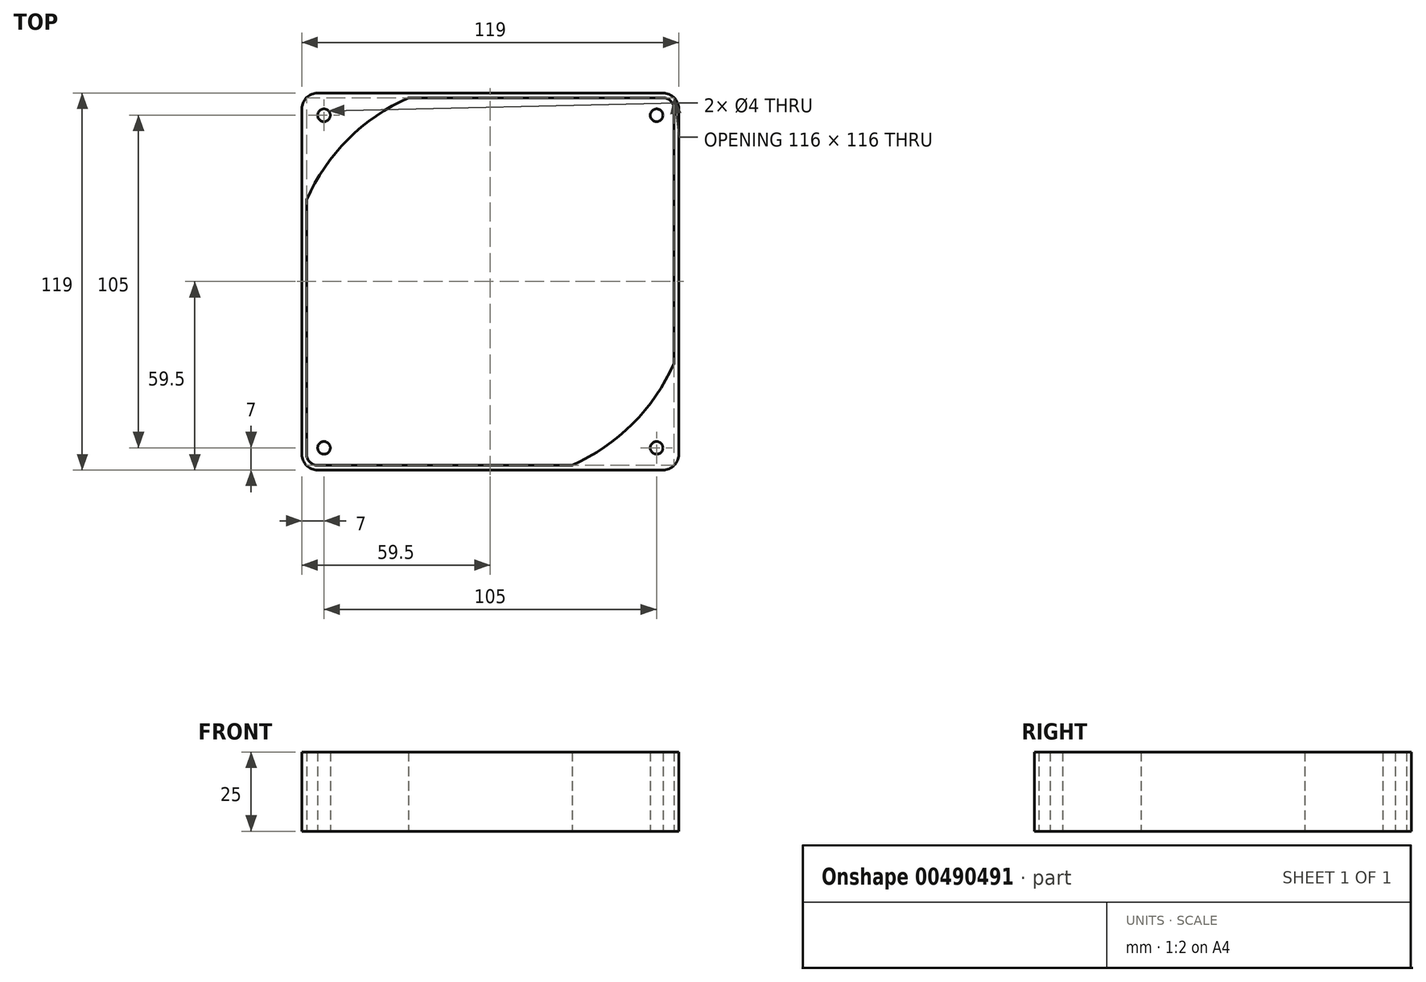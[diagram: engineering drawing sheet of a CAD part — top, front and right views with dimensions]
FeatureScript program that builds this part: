
annotation { "Feature Type Name" : "Feature", "Feature Type Description" : "" }
export const myFeature = defineFeature(function(context is Context, id is Id, definition is map)
    precondition{}
    {
        {
            var Q0;
            Q0=qCreatedBy(makeId("Top.planeOp"),FACE);
            var sketch = newSketch(context, id + "F0", { "sketchPlane" : qUnion([Q0])});
            skLineSegment(sketch, "E0.bottom", {"start": v(-54.5, -59.5) * mm, "end": v(54.5, -59.5) * mm});
            skLineSegment(sketch, "E0.top", {"start": v(-54.5, 59.5) * mm, "end": v(54.5, 59.5) * mm});
            skLineSegment(sketch, "E0.left", {"start": v(-59.5, -54.5) * mm, "end": v(-59.5, 54.5) * mm});
            skLineSegment(sketch, "E0.right", {"start": v(59.5, -54.5) * mm, "end": v(59.5, 54.5) * mm});
            skPoint(sketch, "E0.middle", {"position": v(0, 0) * mm});
            skLineSegment(sketch, "E1", {"start": v(-83.43, 52.5) * mm, "end": v(72.05, 52.5) * mm, "construction": true});
            skLineSegment(sketch, "E2", {"start": v(-59.5, 59.5) * mm, "end": v(59.5, -59.5) * mm, "construction": true});
            skCircle(sketch, "E3", {"center": v(-52.5, 52.5) * mm, "radius": 2 * mm});
            skPoint(sketch, "E4.visualSharp", {"position": v(-59.5, 59.5) * mm});
            skArc(sketch, "E4.filletArc", {"start": v(-54.5, 59.5) * mm, "mid": v(-58.04, 58.04) * mm, "end": v(-59.5, 54.5) * mm});
            skPoint(sketch, "E5.visualSharp", {"position": v(59.5, 59.5) * mm});
            skArc(sketch, "E5.filletArc", {"start": v(59.5, 54.5) * mm, "mid": v(58.04, 58.04) * mm, "end": v(54.5, 59.5) * mm});
            skPoint(sketch, "E6.visualSharp", {"position": v(59.5, -59.5) * mm});
            skArc(sketch, "E6.filletArc", {"start": v(54.5, -59.5) * mm, "mid": v(58.04, -58.04) * mm, "end": v(59.5, -54.5) * mm});
            skPoint(sketch, "E7.visualSharp", {"position": v(-59.5, -59.5) * mm});
            skArc(sketch, "E7.filletArc", {"start": v(-59.5, -54.5) * mm, "mid": v(-58.04, -58.04) * mm, "end": v(-54.5, -59.5) * mm});
            skCircle(sketch, "E8.MirrorC", {"center": v(-52.5, -52.5) * mm, "radius": 2 * mm});
            skCircle(sketch, "E9.MirrorC", {"center": v(52.5, 52.5) * mm, "radius": 2 * mm});
            skCircle(sketch, "E10.MirrorC", {"center": v(52.5, -52.5) * mm, "radius": 2 * mm});
            skArc(sketch, "E11.0", {"start": v(-54.5, 58) * mm, "mid": v(-56.97, 56.97) * mm, "end": v(-58, 54.5) * mm});
            skLineSegment(sketch, "E11.1", {"start": v(-58, -54.5) * mm, "end": v(-58, 54.5) * mm});
            skLineSegment(sketch, "E11.2", {"start": v(-54.5, 58) * mm, "end": v(54.5, 58) * mm});
            skArc(sketch, "E11.3", {"start": v(-58, -54.5) * mm, "mid": v(-56.97, -56.97) * mm, "end": v(-54.5, -58) * mm});
            skArc(sketch, "E11.4", {"start": v(58, 54.5) * mm, "mid": v(56.97, 56.97) * mm, "end": v(54.5, 58) * mm});
            skLineSegment(sketch, "E11.5", {"start": v(58, -54.5) * mm, "end": v(58, 54.5) * mm});
            skArc(sketch, "E11.6", {"start": v(54.5, -58) * mm, "mid": v(56.97, -56.97) * mm, "end": v(58, -54.5) * mm});
            skLineSegment(sketch, "E11.7", {"start": v(-54.5, -58) * mm, "end": v(54.5, -58) * mm});
            skCircle(sketch, "E12", {"center": v(0, 0) * mm, "radius": 58 * mm});
            skPoint(sketch, "E12.first.point", {"position": v(-58, 0) * mm});
            skPoint(sketch, "E12.second.point", {"position": v(0, -58) * mm});
            skPoint(sketch, "E12.third.point", {"position": v(58, 0) * mm});
            skCircle(sketch, "E13", {"center": v(0, 0) * mm, "radius": 63.5 * mm});
            skSolve(sketch);
        }
        {
            var Q0;
            Q0=makeQuery(id+"F0.imprint","IMPRINT",FACE,{"disambiguationData":[TD([[makeQuery(id+"F0.imprint","IMPRINT",EDGE,{"derivedFrom":sQuery(id+"F0.wireOp",EDGE,"E3")}),-1.0]])]});
            var Q1;
            {var subQ1=sQuery(id+"F0.wireOp",EDGE,"E4.filletArc");Q1=makeQuery(id+"F0.imprint","IMPRINT",FACE,{"disambiguationData":[TD([[makeQuery(id+"F0.imprint","IMPRINT",EDGE,{"derivedFrom":subQ1}),1.0]])]});}
            var Q2;
            {var subQ0=sQuery(id+"F0.wireOp",EDGE,"E13");var subQ1=sQuery(id+"F0.wireOp",EDGE,"E0.left");var subQ7=makeQuery(id+"F0.imprint","INTERSECT",VERTEX,{"disambiguationData":[OD(0.0)],"derivedFrom":[subQ1,subQ0]});Q2=makeQuery(id+"F0.imprint","IMPRINT",FACE,{"disambiguationData":[TD([[makeQuery(id+"F0.imprint","IMPRINT",EDGE,{"disambiguationData":[TD([[subQ7,-1.0]])],"derivedFrom":subQ1}),-1.0]])]});}
            var Q3;
            {var subQ8=sQuery(id+"F0.wireOp",EDGE,"E7.filletArc");Q3=makeQuery(id+"F0.imprint","IMPRINT",FACE,{"disambiguationData":[TD([[makeQuery(id+"F0.imprint","IMPRINT",EDGE,{"derivedFrom":subQ8}),1.0]])]});}
            var Q4;
            {var subQ2=sQuery(id+"F0.wireOp",EDGE,"E13");var subQ4=sQuery(id+"F0.wireOp",EDGE,"E0.top");var subQ7=makeQuery(id+"F0.imprint","INTERSECT",VERTEX,{"disambiguationData":[OD(0.0)],"derivedFrom":[subQ4,subQ2]});Q4=makeQuery(id+"F0.imprint","IMPRINT",FACE,{"disambiguationData":[TD([[makeQuery(id+"F0.imprint","IMPRINT",EDGE,{"disambiguationData":[TD([[subQ7,-1.0]])],"derivedFrom":subQ4}),-1.0]])]});}
            var Q5;
            {var subQ4=sQuery(id+"F0.wireOp",EDGE,"E5.filletArc");Q5=makeQuery(id+"F0.imprint","IMPRINT",FACE,{"disambiguationData":[TD([[makeQuery(id+"F0.imprint","IMPRINT",EDGE,{"derivedFrom":subQ4}),1.0]])]});}
            var Q6;
            Q6=makeQuery(id+"F0.imprint","IMPRINT",FACE,{"disambiguationData":[TD([[makeQuery(id+"F0.imprint","IMPRINT",EDGE,{"derivedFrom":sQuery(id+"F0.wireOp",EDGE,"E9.MirrorC")}),1.0]])]});
            var Q7;
            {var subQ0=sQuery(id+"F0.wireOp",EDGE,"E13");var subQ1=sQuery(id+"F0.wireOp",EDGE,"E0.right");var subQ7=makeQuery(id+"F0.imprint","INTERSECT",VERTEX,{"disambiguationData":[OD(0.0)],"derivedFrom":[subQ1,subQ0]});Q7=makeQuery(id+"F0.imprint","IMPRINT",FACE,{"disambiguationData":[TD([[makeQuery(id+"F0.imprint","IMPRINT",EDGE,{"disambiguationData":[TD([[subQ7,-1.0]])],"derivedFrom":subQ1}),1.0]])]});}
            var Q8;
            {var subQ4=sQuery(id+"F0.wireOp",EDGE,"E6.filletArc");Q8=makeQuery(id+"F0.imprint","IMPRINT",FACE,{"disambiguationData":[TD([[makeQuery(id+"F0.imprint","IMPRINT",EDGE,{"derivedFrom":subQ4}),1.0]])]});}
            var Q9;
            {var subQ0=sQuery(id+"F0.wireOp",EDGE,"E13");var subQ1=sQuery(id+"F0.wireOp",EDGE,"E0.bottom");var subQ2=makeQuery(id+"F0.imprint","INTERSECT",VERTEX,{"disambiguationData":[OD(0.0)],"derivedFrom":[subQ1,subQ0]});Q9=makeQuery(id+"F0.imprint","IMPRINT",FACE,{"disambiguationData":[TD([[makeQuery(id+"F0.imprint","IMPRINT",EDGE,{"disambiguationData":[TD([[subQ2,-1.0]])],"derivedFrom":subQ1}),1.0]])]});}
            var Q10;
            Q10=makeQuery(id+"F0.imprint","IMPRINT",FACE,{"disambiguationData":[TD([[makeQuery(id+"F0.imprint","IMPRINT",EDGE,{"derivedFrom":sQuery(id+"F0.wireOp",EDGE,"E10.MirrorC")}),-1.0]])]});
            var Q11;
            Q11=makeQuery(id+"F0.imprint","IMPRINT",FACE,{"disambiguationData":[TD([[makeQuery(id+"F0.imprint","IMPRINT",EDGE,{"derivedFrom":sQuery(id+"F0.wireOp",EDGE,"E8.MirrorC")}),1.0]])]});
            extrude(context, id + "F1", {"entities" : qUnion([Q0, Q1, Q2, Q3, Q4, Q5, Q6, Q7, Q8, Q9, Q10, Q11]), "depth" : 25 * mm});
        }
    });
